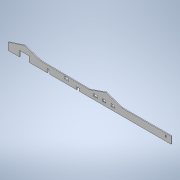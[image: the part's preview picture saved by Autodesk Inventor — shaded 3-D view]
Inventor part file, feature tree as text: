
AUTODESK INVENTOR PART (.ipt)
format: ipt  version: 2020.1 (Build 241239000, 239)  size: 176,128 bytes
history: native  units: in
note: dims shown in document units (in); Inventor stores cm internally (conversion verified against a paired STEP export)
features: extrude x1, sketch x1
ambient origin geometry x8: Origin, YZ Plane, XZ Plane, XY Plane, X Axis, Y Axis, Z Axis, Center Point
bodies: Body1 (feature_tree)
feature tree (2):
  extrude  "Extrusion2"  Depth=168.0in
  sketch  "Sketch1"  dims[d0=103.0in d1=168.0in d2=84.0in d3=143.0in d4=167.0in d5=102.0in d6=720.0in d7=96.0in d8=38.0in d9=36.0in d10=60.0in d11=180.0in d12=480.0in d13=100.0in d14=180.0in d15=60.0in d16=35.0in d17=48.0in d18=35.0in d19=48.0in d20=35.0in d21=722.0in d22=103.0in d23=15.0in d24=27.0in d27=40.0in d28=39.0in d29=150.0in d30=121.0in d31=12.0in d32=0.0in d33=2400.0in d34=251.0976in d35=251.0976in d36=720.0in d37=254.2754in d38=252.9822in d39=722.0in]
